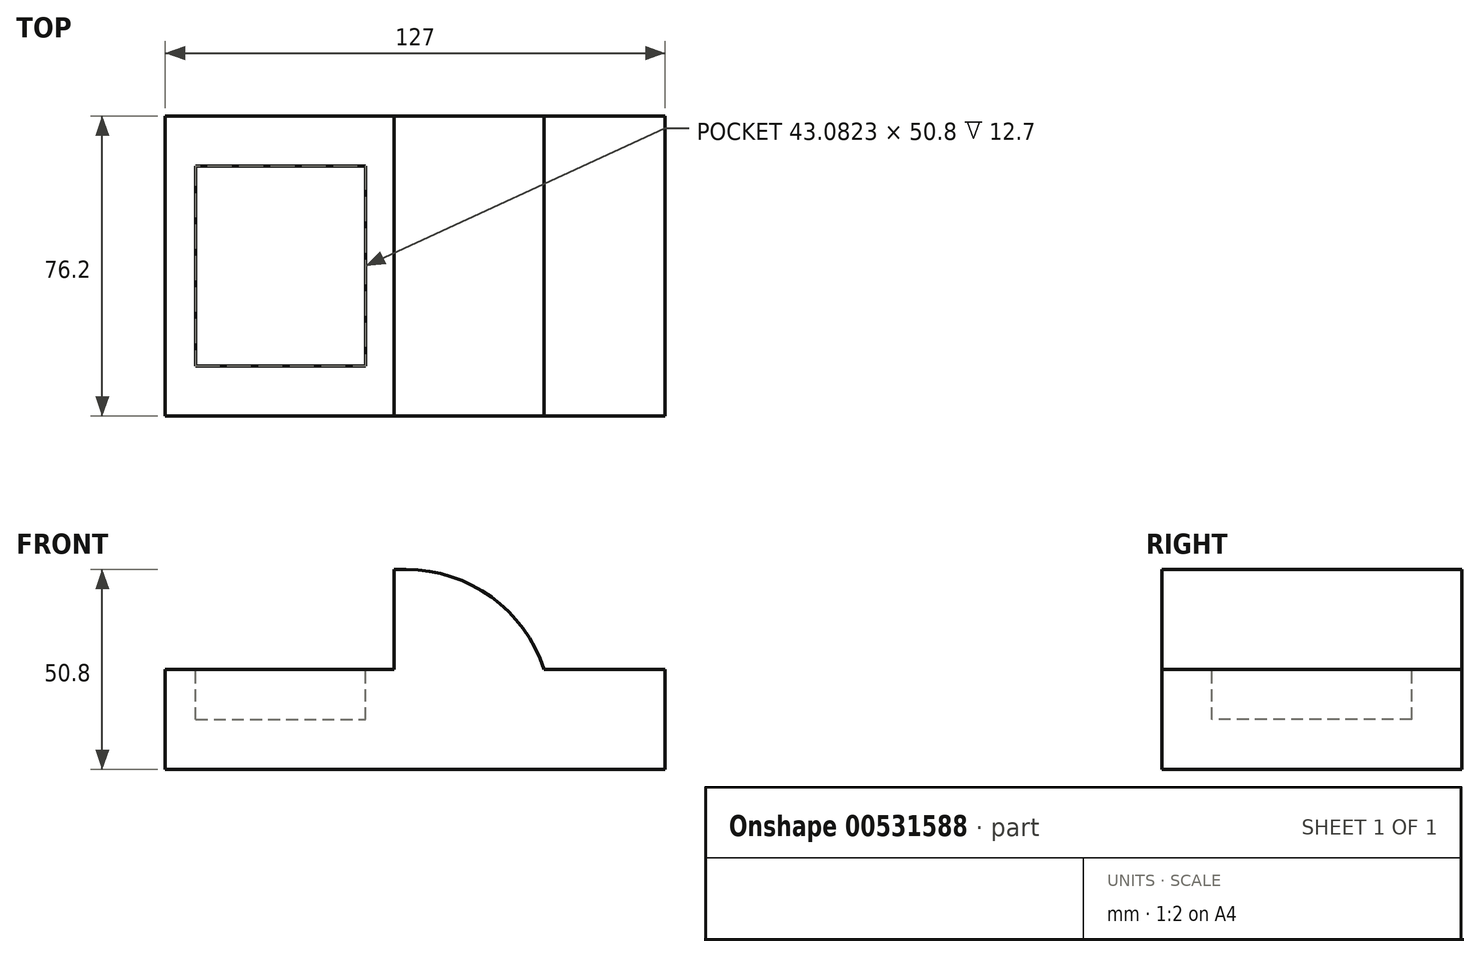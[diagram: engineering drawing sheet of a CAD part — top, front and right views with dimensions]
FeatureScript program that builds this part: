
annotation { "Feature Type Name" : "Feature", "Feature Type Description" : "" }
export const myFeature = defineFeature(function(context is Context, id is Id, definition is map)
    precondition{}
    {
        {
            var Q0;
            Q0=qCreatedBy(makeId("Top.planeOp"),FACE);
            var sketch = newSketch(context, id + "F0", { "sketchPlane" : qUnion([Q0])});
            skLineSegment(sketch, "E0.bottom", {"start": v(-68.45, 35.72) * mm, "end": v(58.55, 35.72) * mm});
            skLineSegment(sketch, "E0.top", {"start": v(-68.45, -40.48) * mm, "end": v(58.55, -40.48) * mm});
            skLineSegment(sketch, "E0.left", {"start": v(-68.45, 35.72) * mm, "end": v(-68.45, -40.48) * mm});
            skLineSegment(sketch, "E0.right", {"start": v(58.55, 35.72) * mm, "end": v(58.55, -40.48) * mm});
            skSolve(sketch);
        }
        {
            var Q0;
            Q0 = qSketchRegion(id + "F0", true);
            extrude(context, id + "F1", {"entities" : qUnion([Q0]), "depth" : 25.4 * mm, "offsetDistance" : 25.4 * mm});
        }
        {
            var Q0;
            Q0=makeQuery(id+"F1.opExtrude","CAP_FACE",FACE,{"disambiguationData":[OSD([sQuery(id+"F0.wireOp",EDGE,"E0.bottom"),sQuery(id+"F0.wireOp",EDGE,"E0.top"),sQuery(id+"F0.wireOp",EDGE,"E0.left"),sQuery(id+"F0.wireOp",EDGE,"E0.right")])],"isStart":false});
            var sketch = newSketch(context, id + "F2", { "sketchPlane" : qUnion([Q0])});
            skLineSegment(sketch, "E1.bottom", {"start": v(-10.35, 35.72) * mm, "end": v(27.75, 35.72) * mm});
            skLineSegment(sketch, "E1.top", {"start": v(-10.35, -40.48) * mm, "end": v(27.75, -40.48) * mm});
            skLineSegment(sketch, "E1.left", {"start": v(-10.35, 35.72) * mm, "end": v(-10.35, -40.48) * mm});
            skLineSegment(sketch, "E1.right", {"start": v(27.75, 35.72) * mm, "end": v(27.75, -40.48) * mm});
            skSolve(sketch);
        }
        {
            var Q0;
            Q0 = qSketchRegion(id + "F2", true);
            extrude(context, id + "F3", {"entities" : qUnion([Q0]), "operationType" : NewBodyOperationType.ADD, "depth" : 25.4 * mm, "offsetDistance" : 25.4 * mm});
        }
        {
            var Q0;
            Q0=makeQuery(id+"F3.opExtrude","CAP_EDGE",EDGE,{"disambiguationData":[OSD([sQuery(id+"F2.wireOp",EDGE,"E1.right")])],"isStart":false});
            fillet(context, id + "F4", {"entities" : qUnion([Q0]), "radius" : 36.8 * mm, "tangentPropagation" : true, "allowEdgeOverflow" : false});
        }
        {
            var Q0;
            {var subQ0=sQuery(id+"F0.wireOp",EDGE,"E0.left");var subQ1=sQuery(id+"F0.wireOp",EDGE,"E0.top");var subQ2=sQuery(id+"F0.wireOp",EDGE,"E0.bottom");Q0=makeQuery(id+"F3.boolean.opBoolean","SPLIT",FACE,{"disambiguationData":[TD([makeQuery(id+"F1.opExtrude","SWEPT_FACE",FACE,{"disambiguationData":[OSD([subQ0])]})])],"derivedFrom":makeQuery(id+"F1.opExtrude","CAP_FACE",FACE,{"disambiguationData":[OSD([subQ2,subQ1,subQ0,sQuery(id+"F0.wireOp",EDGE,"E0.right")])],"isStart":false})});}
            var sketch = newSketch(context, id + "F5", { "sketchPlane" : qUnion([Q0])});
            skLineSegment(sketch, "E2", {"start": v(-39.4, 35.72) * mm, "end": v(-39.4, 23.02) * mm});
            skLineSegment(sketch, "E3", {"start": v(-39.4, -40.48) * mm, "end": v(-39.4, -27.78) * mm});
            skLineSegment(sketch, "E4.bottom", {"start": v(-60.7, 23.02) * mm, "end": v(-17.62, 23.02) * mm});
            skLineSegment(sketch, "E4.top", {"start": v(-60.7, -27.78) * mm, "end": v(-17.62, -27.78) * mm});
            skLineSegment(sketch, "E4.left", {"start": v(-60.7, 23.02) * mm, "end": v(-60.7, -27.78) * mm});
            skLineSegment(sketch, "E4.right", {"start": v(-17.62, 23.02) * mm, "end": v(-17.62, -27.78) * mm});
            skSolve(sketch);
        }
        {
            var Q0;
            Q0 = qSketchRegion(id + "F5", true);
            extrude(context, id + "F6", {"entities" : qUnion([Q0]), "operationType" : NewBodyOperationType.REMOVE, "oppositeDirection" : true, "depth" : 12.7 * mm, "offsetDistance" : 25.4 * mm});
        }
    });
